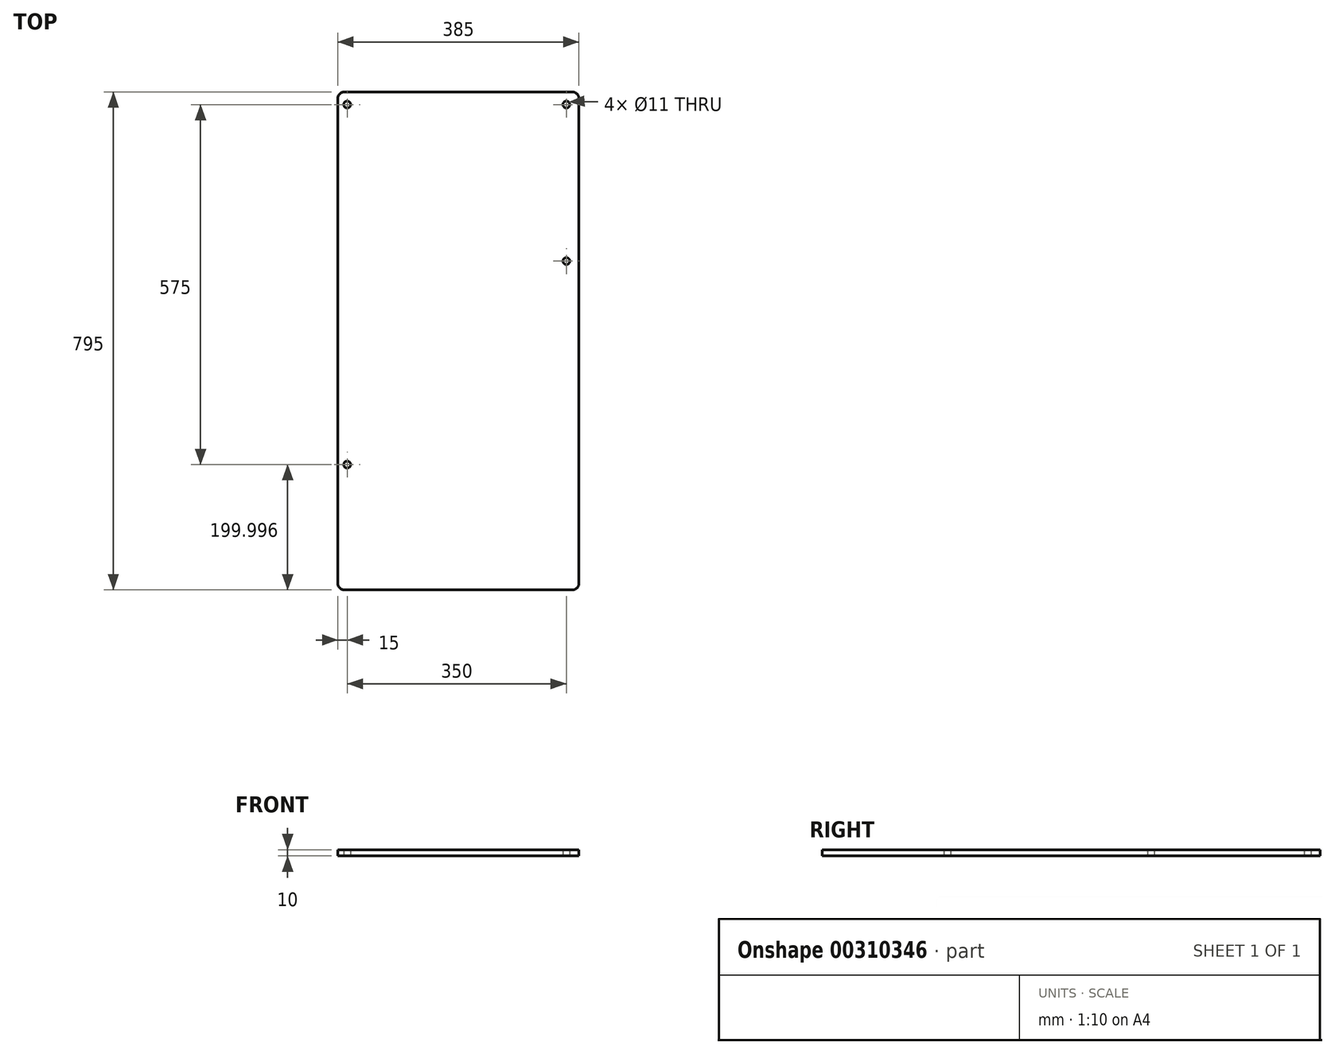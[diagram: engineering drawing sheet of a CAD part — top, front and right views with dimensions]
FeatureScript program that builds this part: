
annotation { "Feature Type Name" : "Feature", "Feature Type Description" : "" }
export const myFeature = defineFeature(function(context is Context, id is Id, definition is map)
    precondition{}
    {
        {
            var Q0;
            Q0=qCreatedBy(makeId("Top.planeOp"),FACE);
            var sketch = newSketch(context, id + "F0", { "sketchPlane" : qUnion([Q0])});
            skLineSegment(sketch, "E0.bottom", {"start": v(-198.65, 600.44) * mm, "end": v(166.35, 600.44) * mm});
            skLineSegment(sketch, "E0.top", {"start": v(-198.65, -194.56) * mm, "end": v(166.35, -194.56) * mm});
            skLineSegment(sketch, "E0.left", {"start": v(-208.65, 590.44) * mm, "end": v(-208.65, -184.56) * mm});
            skLineSegment(sketch, "E0.right", {"start": v(176.35, 590.44) * mm, "end": v(176.35, -184.56) * mm});
            skCircle(sketch, "E1", {"center": v(-193.65, 5.44) * mm, "radius": 5.5 * mm});
            skCircle(sketch, "E2", {"center": v(156.35, 330.44) * mm, "radius": 5.5 * mm});
            skCircle(sketch, "E3", {"center": v(156.35, 580.44) * mm, "radius": 5.5 * mm});
            skCircle(sketch, "E4", {"center": v(-193.65, 580.44) * mm, "radius": 5.5 * mm});
            skLineSegment(sketch, "E5", {"start": v(-289.99, 811.19) * mm, "end": v(270.01, 811.19) * mm});
            skLineSegment(sketch, "E6", {"start": v(270.01, 811.19) * mm, "end": v(270.01, 771.19) * mm});
            skLineSegment(sketch, "E7", {"start": v(270.01, 771.19) * mm, "end": v(210.01, 771.19) * mm});
            skLineSegment(sketch, "E8", {"start": v(210.01, 771.19) * mm, "end": v(210.01, 811.19) * mm});
            skLineSegment(sketch, "E9", {"start": v(-289.99, 811.19) * mm, "end": v(-289.99, 771.19) * mm});
            skLineSegment(sketch, "E10", {"start": v(-289.99, 771.19) * mm, "end": v(-229.99, 771.19) * mm});
            skLineSegment(sketch, "E11", {"start": v(-229.99, 771.19) * mm, "end": v(-229.99, 811.19) * mm});
            skPoint(sketch, "E12.visualSharp", {"position": v(-208.65, 600.44) * mm});
            skArc(sketch, "E12.filletArc", {"start": v(-198.65, 600.44) * mm, "mid": v(-205.72, 597.5) * mm, "end": v(-208.65, 590.44) * mm});
            skPoint(sketch, "E13.visualSharp", {"position": v(176.35, 600.44) * mm});
            skArc(sketch, "E13.filletArc", {"start": v(176.35, 590.44) * mm, "mid": v(173.42, 597.5) * mm, "end": v(166.35, 600.44) * mm});
            skPoint(sketch, "E14.visualSharp", {"position": v(176.35, -194.56) * mm});
            skArc(sketch, "E14.filletArc", {"start": v(166.35, -194.56) * mm, "mid": v(173.42, -191.64) * mm, "end": v(176.35, -184.56) * mm});
            skPoint(sketch, "E15.visualSharp", {"position": v(-208.65, -194.56) * mm});
            skArc(sketch, "E15.filletArc", {"start": v(-208.65, -184.56) * mm, "mid": v(-205.72, -191.64) * mm, "end": v(-198.65, -194.56) * mm});
            skSolve(sketch);
        }
        {
            var Q0;
            Q0=makeQuery(id+"F0.imprint","IMPRINT",FACE,{"disambiguationData":[TD([[makeQuery(id+"F0.imprint","IMPRINT",EDGE,{"derivedFrom":sQuery(id+"F0.wireOp",EDGE,"E0.bottom")}),-1.0]])]});
            extrude(context, id + "F1", {"entities" : qUnion([Q0]), "depth" : 10 * mm});
        }
    });
